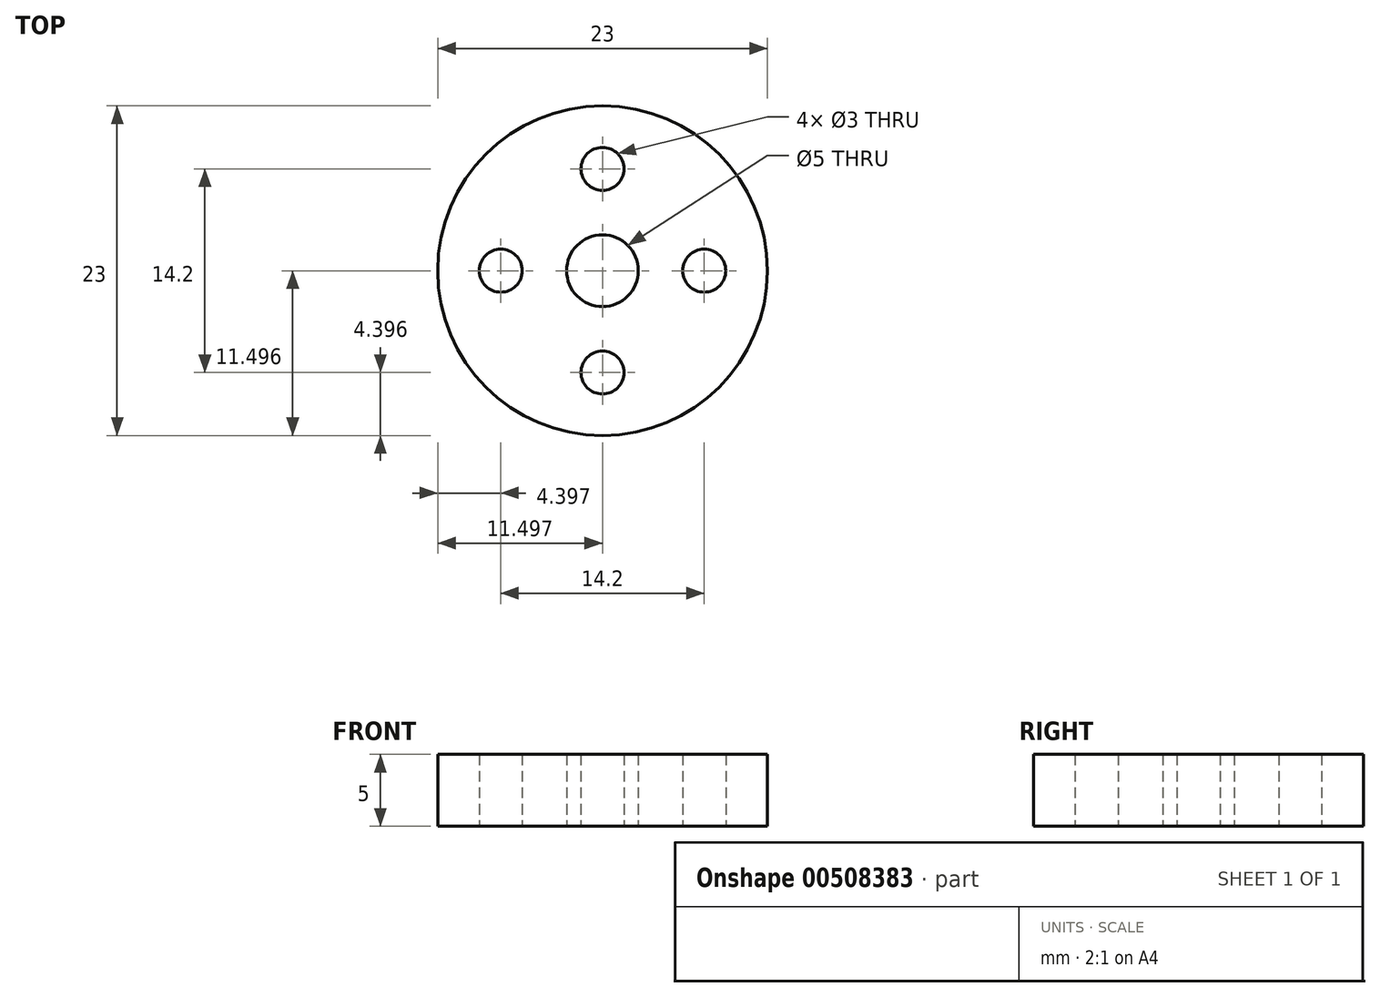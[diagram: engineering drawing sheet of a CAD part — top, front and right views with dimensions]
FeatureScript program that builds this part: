
annotation { "Feature Type Name" : "Feature", "Feature Type Description" : "" }
export const myFeature = defineFeature(function(context is Context, id is Id, definition is map)
    precondition{}
    {
        {
            var Q0;
            Q0=qCreatedBy(makeId("Top.planeOp"),FACE);
            var sketch = newSketch(context, id + "F0", { "sketchPlane" : qUnion([Q0])});
            skCircle(sketch, "E0", {"center": v(-55.44, 4.88) * mm, "radius": 11.5 * mm});
            skCircle(sketch, "E1", {"center": v(-55.44, 4.88) * mm, "radius": 2.5 * mm});
            skCircle(sketch, "E2", {"center": v(-48.34, 4.88) * mm, "radius": 1.5 * mm});
            skCircle(sketch, "E3.1.0", {"center": v(-55.44, 11.98) * mm, "radius": 1.5 * mm});
            skCircle(sketch, "E3.2.0", {"center": v(-62.54, 4.88) * mm, "radius": 1.5 * mm});
            skCircle(sketch, "E4.1.3.0", {"center": v(-55.44, -2.22) * mm, "radius": 1.5 * mm});
            skSolve(sketch);
        }
        {
            var Q0;
            Q0=makeQuery(id+"F0.imprint","IMPRINT",FACE,{"disambiguationData":[TD([[makeQuery(id+"F0.imprint","IMPRINT",EDGE,{"derivedFrom":sQuery(id+"F0.wireOp",EDGE,"E0")}),1.0]])]});
            var Q1;
            Q1=sQuery(id+"F0.wireOp",EDGE,"E0");
            extrude(context, id + "F1", {"entities" : qUnion([Q0]), "surfaceEntities" : qUnion([Q1]), "depth" : 5 * mm});
        }
    });
